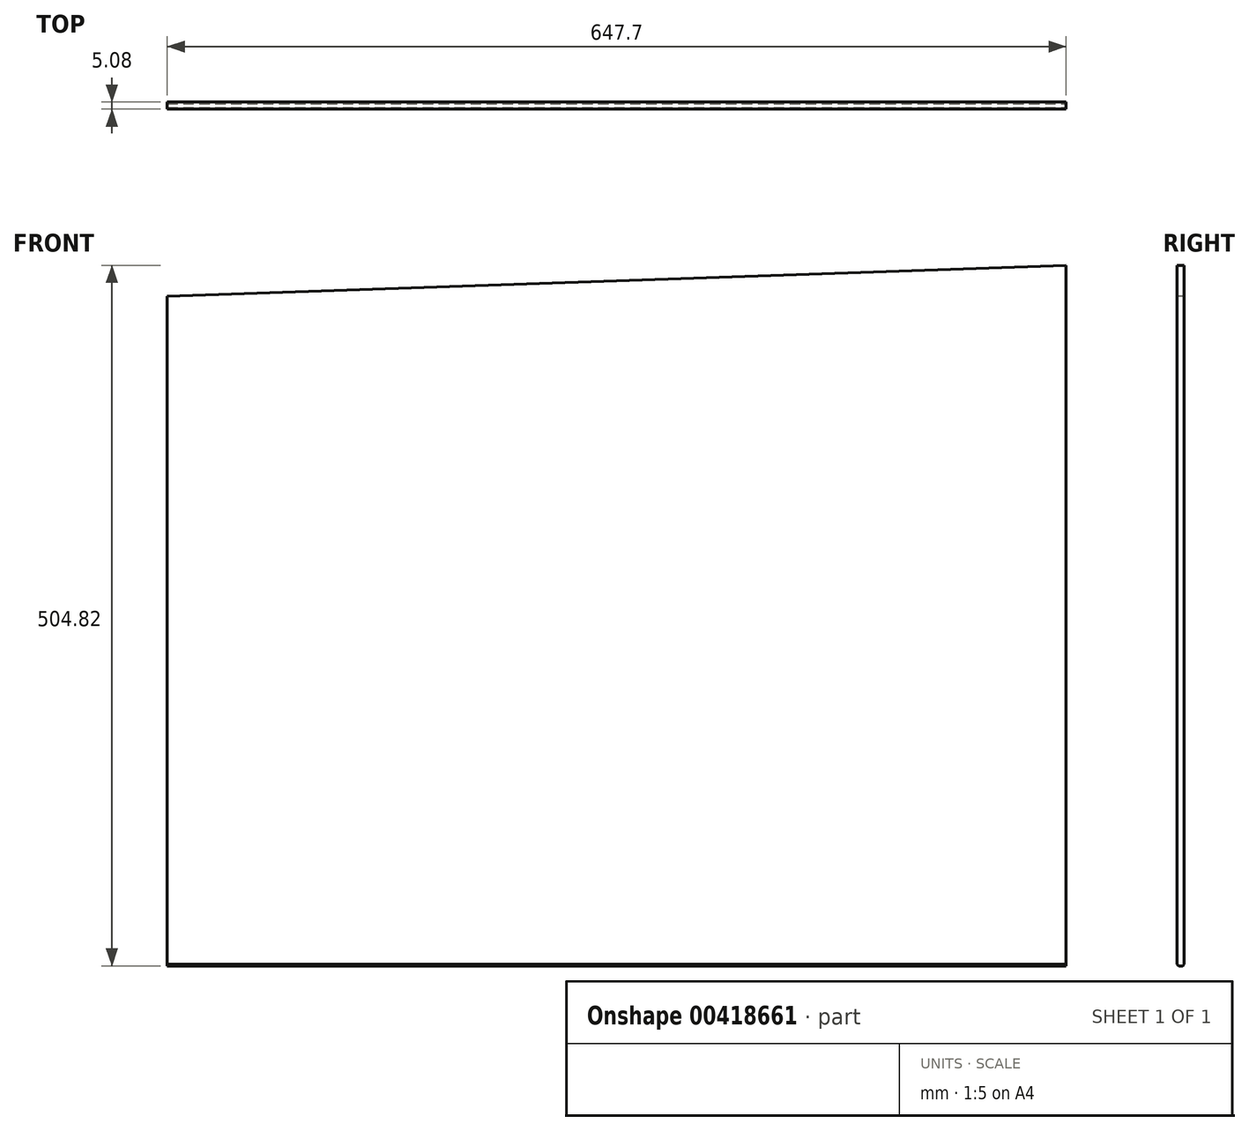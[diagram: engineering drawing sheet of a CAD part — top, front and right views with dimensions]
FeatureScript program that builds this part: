
annotation { "Feature Type Name" : "Feature", "Feature Type Description" : "" }
export const myFeature = defineFeature(function(context is Context, id is Id, definition is map)
    precondition{}
    {
        {
            var Q0;
            Q0=qCreatedBy(makeId("Front.planeOp"),FACE);
            var sketch = newSketch(context, id + "F0", { "sketchPlane" : qUnion([Q0])});
            skLineSegment(sketch, "E0", {"start": v(0, 0) * mm, "end": v(0, 482.6) * mm});
            skLineSegment(sketch, "E1", {"start": v(0, 0) * mm, "end": v(647.7, 0) * mm});
            skLineSegment(sketch, "E2", {"start": v(647.7, 0) * mm, "end": v(647.7, 504.83) * mm});
            skLineSegment(sketch, "E3", {"start": v(647.7, 504.83) * mm, "end": v(0, 482.6) * mm});
            skSolve(sketch);
        }
        {
            var Q0;
            Q0 = qSketchRegion(id + "F0", true);
            extrude(context, id + "F1", {"entities" : qUnion([Q0]), "oppositeDirection" : true, "depth" : 5.08 * mm});
        }
        {
            var Q0;
            Q0=makeQuery(id+"F1.opExtrude","SWEPT_FACE",FACE,{"disambiguationData":[OSD([sQuery(id+"F0.wireOp",EDGE,"E2")])]});
            var sketch = newSketch(context, id + "F2", { "sketchPlane" : qUnion([Q0])});
            skLineSegment(sketch, "E4", {"start": v(0, 0) * mm, "end": v(1.12, 0) * mm});
            skLineSegment(sketch, "E5", {"start": v(1.12, 0) * mm, "end": v(0, 1.12) * mm});
            skLineSegment(sketch, "E6", {"start": v(0, 1.12) * mm, "end": v(0, 0) * mm});
            skLineSegment(sketch, "E7", {"start": v(5.08, 0) * mm, "end": v(3.95, 0) * mm});
            skLineSegment(sketch, "E8", {"start": v(3.95, 0) * mm, "end": v(5.08, 1.12) * mm});
            skLineSegment(sketch, "E9", {"start": v(5.08, 1.12) * mm, "end": v(5.08, 0) * mm});
            skSolve(sketch);
        }
        {
            var Q0;
            Q0=makeQuery(id+"F2.imprint","IMPRINT",FACE,{"disambiguationData":[TD([[makeQuery(id+"F2.imprint","IMPRINT",EDGE,{"derivedFrom":sQuery(id+"F2.wireOp",EDGE,"E7")}),-1.0]])]});
            var Q1;
            Q1=makeQuery(id+"F2.imprint","IMPRINT",FACE,{"disambiguationData":[TD([[makeQuery(id+"F2.imprint","IMPRINT",EDGE,{"derivedFrom":sQuery(id+"F2.wireOp",EDGE,"E4")}),-1.0]])]});
            extrude(context, id + "F3", {"entities" : qUnion([Q0, Q1]), "operationType" : NewBodyOperationType.REMOVE, "oppositeDirection" : true, "depth" : 751.84 * mm});
        }
    });
